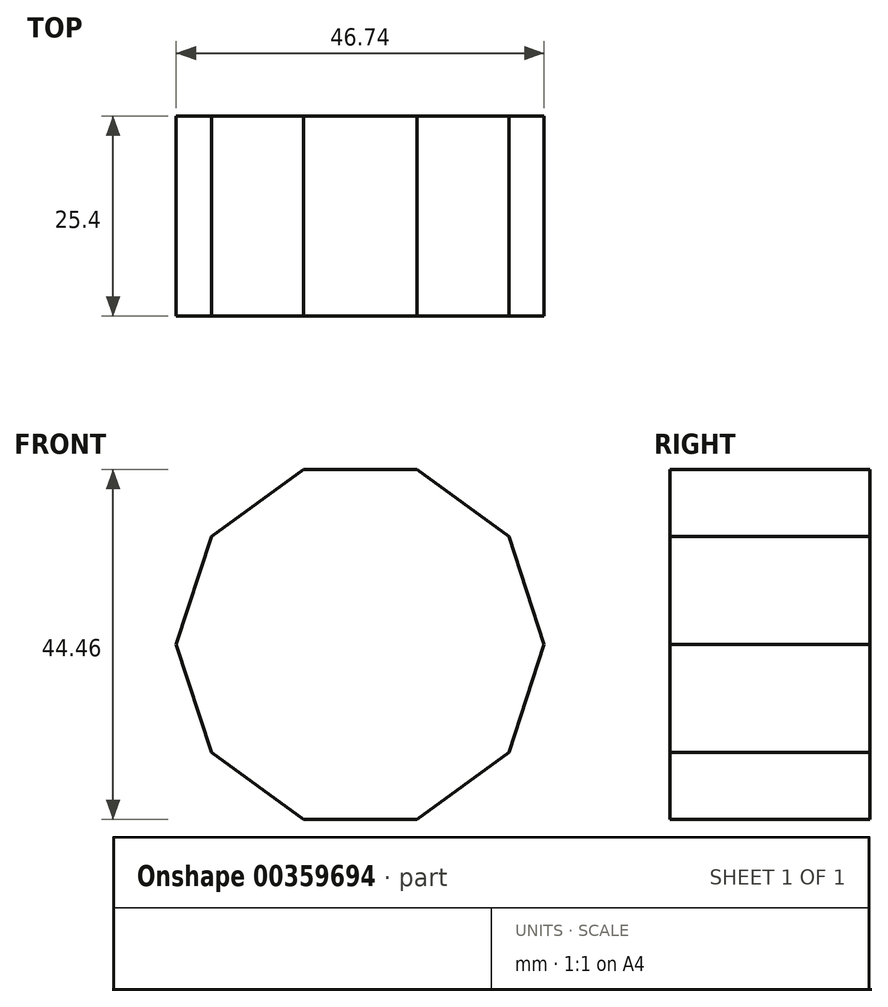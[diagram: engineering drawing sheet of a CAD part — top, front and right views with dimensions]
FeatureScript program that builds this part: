
annotation { "Feature Type Name" : "Feature", "Feature Type Description" : "" }
export const myFeature = defineFeature(function(context is Context, id is Id, definition is map)
    precondition{}
    {
        {
            var Q0;
            Q0=qCreatedBy(makeId("Front.planeOp"),FACE);
            var sketch = newSketch(context, id + "F0", { "sketchPlane" : qUnion([Q0])});
            skLineSegment(sketch, "E0", {"start": v(0, 0) * mm, "end": v(0, 22.23) * mm});
            skCircle(sketch, "E1.cCircle", {"center": v(0, 0) * mm, "radius": 22.23 * mm, "construction": true});
            skLineSegment(sketch, "E1.0", {"start": v(-7.22, 22.23) * mm, "end": v(7.22, 22.23) * mm});
            skLineSegment(sketch, "E1.1", {"start": v(7.22, 22.23) * mm, "end": v(18.9, 13.74) * mm});
            skLineSegment(sketch, "E1.2", {"start": v(18.9, 13.74) * mm, "end": v(23.37, 0) * mm});
            skLineSegment(sketch, "E1.3", {"start": v(23.37, 0) * mm, "end": v(18.9, -13.74) * mm});
            skLineSegment(sketch, "E1.4", {"start": v(18.9, -13.74) * mm, "end": v(7.22, -22.23) * mm});
            skLineSegment(sketch, "E1.5", {"start": v(7.22, -22.23) * mm, "end": v(-7.22, -22.23) * mm});
            skLineSegment(sketch, "E1.6", {"start": v(-7.22, -22.23) * mm, "end": v(-18.9, -13.74) * mm});
            skLineSegment(sketch, "E1.7", {"start": v(-18.9, -13.74) * mm, "end": v(-23.37, 0) * mm});
            skLineSegment(sketch, "E1.8", {"start": v(-23.37, 0) * mm, "end": v(-18.9, 13.74) * mm});
            skLineSegment(sketch, "E1.9", {"start": v(-18.9, 13.74) * mm, "end": v(-7.22, 22.23) * mm});
            skPoint(sketch, "E1.0.midPoint", {"position": v(0, 22.23) * mm});
            skSolve(sketch);
        }
        {
            var Q0;
            Q0 = qSketchRegion(id + "F0", true);
            extrude(context, id + "F1", {"entities" : qUnion([Q0]), "depth" : 25.4 * mm});
        }
    });
